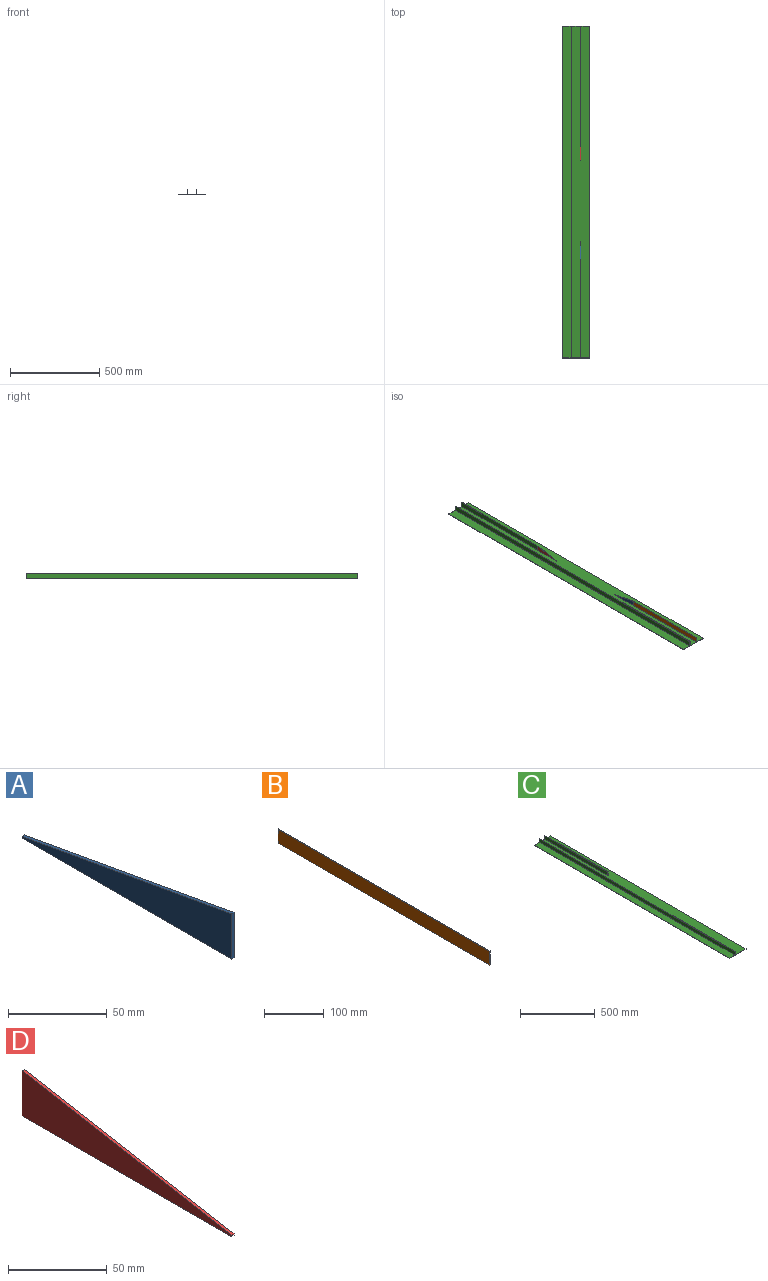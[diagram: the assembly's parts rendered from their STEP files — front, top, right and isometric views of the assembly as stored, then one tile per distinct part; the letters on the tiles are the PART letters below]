
ASSEMBLY  parts=4 mates=9
PART A: 6 faces, bbox 2x150x28 mm
  f0: plane 28x2mm, normal (0,-1,0), area 56mm2, adj f2,f3,f4,f5
  f1: plane 2x1mm, normal (0,1,0), area 2mm2, adj f2,f3,f4,f5
  f2: plane 150x27mm, normal (0,0.18,0.98), area 304.8mm2, adj f0,f1,f3,f5
  f3: plane 150x28mm, normal (1,0,0), area 2175mm2, adj f0,f1,f2,f4
  f4: plane 150x2mm, normal (0,0,-1), area 300mm2, adj f0,f1,f3,f5
  f5: plane 150x28mm, normal (-1,0,0), area 2175mm2, adj f0,f1,f2,f4
PART B: 6 faces, bbox 2x500x28 mm
  f0: plane 500x2mm, normal (0,0,1), area 1000mm2, adj f1,f3,f4,f5
  f1: plane 500x28mm, normal (-1,0,0), area 14000mm2, adj f0,f2,f4,f5
  f2: plane 500x2mm, normal (0,0,-1), area 1000mm2, adj f1,f3,f4,f5
  f3: plane 500x28mm, normal (1,0,0), area 14000mm2, adj f0,f2,f4,f5
  f4: plane 28x2mm, normal (0,1,0), area 56mm2, adj f0,f1,f2,f3
  f5: plane 28x2mm, normal (0,-1,0), area 56mm2, adj f0,f1,f2,f3
PART C: 14 faces, bbox 154x1858x30 mm
  f0: plane 1858x28mm, normal (-1,0,0), area 52024mm2, adj f1,f7,f8,f9
  f1: plane 1858x50mm, normal (0,0,1), area 92900mm2, adj f0,f2,f8,f9
  f2: plane 1858x2mm, normal (-1,0,0), area 3716mm2, adj f1,f3,f8,f9
  f3: plane 1858x154mm, normal (0,0,-1), area 286132mm2, adj f2,f4,f8,f9
  f4: plane 1858x2mm, normal (1,0,0), area 3716mm2, adj f3,f5,f8,f9
  f5: plane 1858x102mm, normal (0,0,1), area 188316mm2, adj f4,f6,f8,f9,f11,f12,f13
  f6: plane 1858x28mm, normal (1,0,0), area 52024mm2, adj f5,f7,f8,f9
  f7: plane 1858x2mm, normal (0,0,1), area 3716mm2, adj f0,f6,f8,f9
  f8: plane 154x30mm, normal (0,-1,0), area 364mm2, adj f0,f1,f2,f3,f4,f5,f6,f7
  f9: plane 154x30mm, normal (0,1,0), area 420mm2, adj f0,f1,f2,f3,f4,f5,f6,f7
  f10: plane 600x2mm, normal (0,0,1), area 1200mm2, adj f9,f11,f12,f13
  f11: plane 600x28mm, normal (-1,0,0), area 16800mm2, adj f5,f9,f10,f13
  f12: plane 600x28mm, normal (1,0,0), area 16800mm2, adj f5,f9,f10,f13
  f13: plane 28x2mm, normal (0,-1,0), area 56mm2, adj f5,f10,f11,f12
PART D: 6 faces, bbox 2x150x28 mm
  f0: plane 28x2mm, normal (0,1,0), area 56mm2, adj f2,f3,f4,f5
  f1: plane 2x1mm, normal (0,-1,0), area 2mm2, adj f2,f3,f4,f5
  f2: plane 150x28mm, normal (-1,0,0), area 2175mm2, adj f0,f1,f3,f5
  f3: plane 150x2mm, normal (0,0,-1), area 300mm2, adj f0,f1,f2,f4
  f4: plane 150x28mm, normal (1,0,0), area 2175mm2, adj f0,f1,f3,f5
  f5: plane 150x27mm, normal (0,-0.18,0.98), area 304.8mm2, adj f0,f1,f2,f4
PLACE A t=(-32.02,-968.37,-24.03)mm
PLACE B t=(-32.02,-968.37,-24.03)mm
PLACE C t=(-32.02,-968.37,-24.03)mm
PLACE D t=(-32.02,-968.37,-24.03)mm
MATE planar A.f0 <-> B.f4  axis (0,-1,0) through (20.98,-2326.37,-8.03)mm
MATE planar A.f4 <-> C.f5  axis (0,0,-1) through (20.98,-2251.37,-22.03)mm
MATE planar D.f3 <-> C.f5  axis (0,0,-1) through (19.98,-1643.37,-22.03)mm
MATE planar C.f12 <-> D.f4  axis (1,0,0) through (21.98,-1268.37,-8.03)mm
MATE planar B.f5 <-> C.f8  axis (0,-1,0) through (20.98,-2826.37,-8.03)mm
MATE planar B.f2 <-> C.f5  axis (0,0,-1) through (20.98,-2576.37,-22.03)mm
MATE planar D.f0 <-> C.f13  axis (0,1,0) through (20.98,-1568.37,-8.03)mm
MATE planar C.f12 <-> B.f3  axis (1,0,0) through (21.98,-1268.37,-8.03)mm
MATE planar B.f3 <-> A.f3  axis (1,0,0) through (21.98,-2576.37,-8.03)mm
